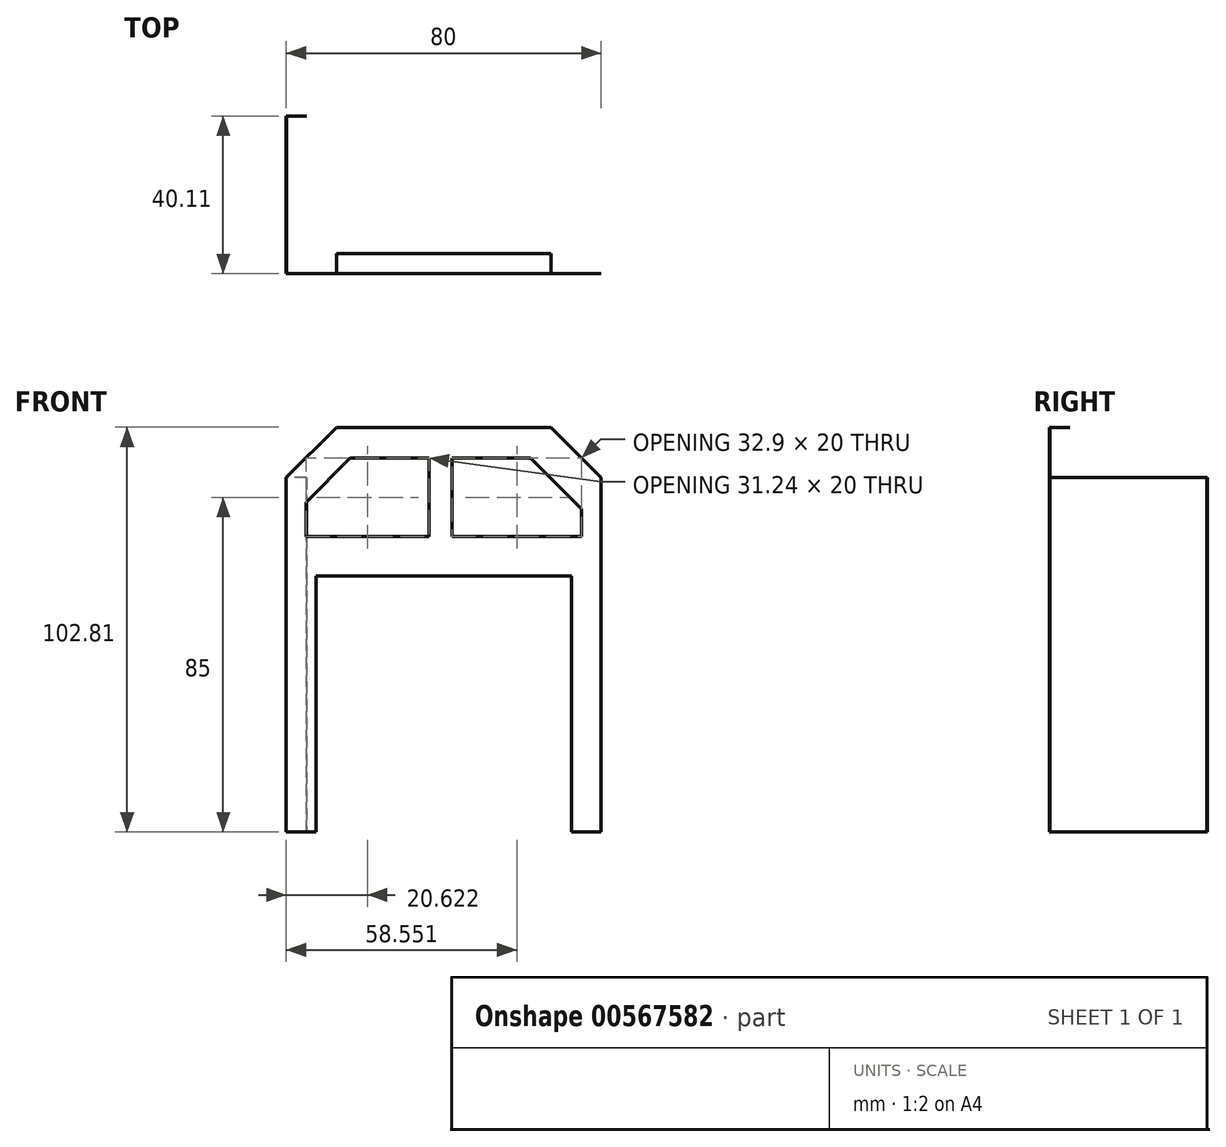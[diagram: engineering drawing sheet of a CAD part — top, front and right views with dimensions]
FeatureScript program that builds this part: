
annotation { "Feature Type Name" : "Feature", "Feature Type Description" : "" }
export const myFeature = defineFeature(function(context is Context, id is Id, definition is map)
    precondition{}
    {
        {
            var Q0;
            Q0=qCreatedBy(makeId("Front.planeOp"),FACE);
            var sketch = newSketch(context, id + "F0", { "sketchPlane" : qUnion([Q0])});
            skLineSegment(sketch, "E0", {"start": v(0, 0) * mm, "end": v(12.8, 12.8) * mm});
            skLineSegment(sketch, "E1", {"start": v(12.8, 12.8) * mm, "end": v(67.2, 12.8) * mm});
            skLineSegment(sketch, "E2", {"start": v(67.2, 12.8) * mm, "end": v(80, 0) * mm});
            skLineSegment(sketch, "E3", {"start": v(80, 0) * mm, "end": v(80, -90) * mm});
            skLineSegment(sketch, "E4", {"start": v(80, -90) * mm, "end": v(72.5, -90) * mm});
            skLineSegment(sketch, "E5", {"start": v(72.5, -90) * mm, "end": v(72.5, -25) * mm});
            skLineSegment(sketch, "E6", {"start": v(72.5, -25) * mm, "end": v(7.5, -25) * mm});
            skLineSegment(sketch, "E7", {"start": v(7.5, -25) * mm, "end": v(7.5, -90) * mm});
            skLineSegment(sketch, "E8", {"start": v(7.5, -90) * mm, "end": v(0, -90) * mm});
            skLineSegment(sketch, "E9", {"start": v(0, -90) * mm, "end": v(0, 0) * mm});
            skLineSegment(sketch, "E10", {"start": v(36.24, 5) * mm, "end": v(36.24, -15) * mm});
            skLineSegment(sketch, "E11", {"start": v(36.24, -15) * mm, "end": v(5, -15) * mm});
            skLineSegment(sketch, "E12", {"start": v(5, -15) * mm, "end": v(5, -6.24) * mm});
            skLineSegment(sketch, "E13", {"start": v(5, -6.24) * mm, "end": v(16.24, 5) * mm});
            skLineSegment(sketch, "E14", {"start": v(16.24, 5) * mm, "end": v(36.24, 5) * mm});
            skLineSegment(sketch, "E15", {"start": v(42.1, 5) * mm, "end": v(42.1, -15) * mm});
            skLineSegment(sketch, "E16", {"start": v(42.1, -15) * mm, "end": v(75, -15) * mm});
            skLineSegment(sketch, "E17", {"start": v(75, -15) * mm, "end": v(75, -7.9) * mm});
            skLineSegment(sketch, "E18", {"start": v(75, -7.9) * mm, "end": v(62.1, 5) * mm});
            skLineSegment(sketch, "E19", {"start": v(62.1, 5) * mm, "end": v(42.1, 5) * mm});
            skSolve(sketch);
        }
        {
            var Q0;
            Q0=makeQuery(id+"F0.imprint","IMPRINT",FACE,{"disambiguationData":[TD([[makeQuery(id+"F0.imprint","IMPRINT",EDGE,{"derivedFrom":sQuery(id+"F0.wireOp",EDGE,"E0")}),-1.0]])]});
            extrude(context, id + "F1", {"entities" : qUnion([Q0]), "depth" : 0.1 * mm, "offsetDistance" : 25 * mm});
        }
        {
            var Q0;
            Q0=makeQuery(id+"F1.opExtrude","CAP_FACE",FACE,{"disambiguationData":[OSD([sQuery(id+"F0.wireOp",EDGE,"E0"),sQuery(id+"F0.wireOp",EDGE,"E1"),sQuery(id+"F0.wireOp",EDGE,"E2"),sQuery(id+"F0.wireOp",EDGE,"E3"),sQuery(id+"F0.wireOp",EDGE,"E4"),sQuery(id+"F0.wireOp",EDGE,"E5"),sQuery(id+"F0.wireOp",EDGE,"E6"),sQuery(id+"F0.wireOp",EDGE,"E7"),sQuery(id+"F0.wireOp",EDGE,"E8"),sQuery(id+"F0.wireOp",EDGE,"E9"),sQuery(id+"F0.wireOp",EDGE,"E10"),sQuery(id+"F0.wireOp",EDGE,"E11"),sQuery(id+"F0.wireOp",EDGE,"E12"),sQuery(id+"F0.wireOp",EDGE,"E13"),sQuery(id+"F0.wireOp",EDGE,"E14"),sQuery(id+"F0.wireOp",EDGE,"E15"),sQuery(id+"F0.wireOp",EDGE,"E16"),sQuery(id+"F0.wireOp",EDGE,"E17"),sQuery(id+"F0.wireOp",EDGE,"E18"),sQuery(id+"F0.wireOp",EDGE,"E19")])],"isStart":true});
            var sketch = newSketch(context, id + "F2", { "sketchPlane" : qUnion([Q0])});
            skLineSegment(sketch, "E20", {"start": v(-79.9, -90) * mm, "end": v(-79.9, 0) * mm});
            skLineSegment(sketch, "E21", {"start": v(-79.89, 0) * mm, "end": v(-80, 0) * mm});
            skLineSegment(sketch, "E22", {"start": v(-80, -90) * mm, "end": v(-79.89, -90) * mm});
            skLineSegment(sketch, "E23", {"start": v(0, -90) * mm, "end": v(-0.1, -90) * mm});
            skLineSegment(sketch, "E24", {"start": v(-0.1, -90) * mm, "end": v(-0.1, 0) * mm});
            skLineSegment(sketch, "E25", {"start": v(-0.1, 0) * mm, "end": v(0, 0) * mm});
            skSolve(sketch);
        }
        {
            var Q0;
            Q0=makeQuery(id+"F2.imprint","IMPRINT",FACE,{"disambiguationData":[TD([[makeQuery(id+"F2.imprint","IMPRINT",EDGE,{"derivedFrom":sQuery(id+"F2.wireOp",EDGE,"E23")}),1.0]])]});
            extrude(context, id + "F3", {"entities" : qUnion([Q0]), "operationType" : NewBodyOperationType.ADD, "depth" : 40 * mm, "offsetDistance" : 25 * mm});
        }
        {
            var Q0;
            Q0=makeQuery(id+"F3.opExtrude","SWEPT_FACE",FACE,{"disambiguationData":[OSD([sQuery(id+"F2.wireOp",EDGE,"E24")])]});
            var sketch = newSketch(context, id + "F4", { "sketchPlane" : qUnion([Q0])});
            skLineSegment(sketch, "E26", {"start": v(40, 0) * mm, "end": v(39.89, 0) * mm});
            skLineSegment(sketch, "E27", {"start": v(39.89, 0) * mm, "end": v(39.9, -90) * mm});
            skSolve(sketch);
        }
        {
            var Q0;
            Q0=makeQuery(id+"F4.imprint","IMPRINT",FACE,{"disambiguationData":[TD([[makeQuery(id+"F4.imprint","IMPRINT",EDGE,{"derivedFrom":sQuery(id+"F4.wireOp",EDGE,"E26")}),1.0]])]});
            extrude(context, id + "F5", {"entities" : qUnion([Q0]), "operationType" : NewBodyOperationType.ADD, "depth" : 5 * mm, "offsetDistance" : 25 * mm});
        }
        {
            var Q0;
            Q0=makeQuery(id+"F1.opExtrude","CAP_FACE",FACE,{"disambiguationData":[OSD([sQuery(id+"F0.wireOp",EDGE,"E0"),sQuery(id+"F0.wireOp",EDGE,"E1"),sQuery(id+"F0.wireOp",EDGE,"E2"),sQuery(id+"F0.wireOp",EDGE,"E3"),sQuery(id+"F0.wireOp",EDGE,"E4"),sQuery(id+"F0.wireOp",EDGE,"E5"),sQuery(id+"F0.wireOp",EDGE,"E6"),sQuery(id+"F0.wireOp",EDGE,"E7"),sQuery(id+"F0.wireOp",EDGE,"E8"),sQuery(id+"F0.wireOp",EDGE,"E9"),sQuery(id+"F0.wireOp",EDGE,"E10"),sQuery(id+"F0.wireOp",EDGE,"E11"),sQuery(id+"F0.wireOp",EDGE,"E12"),sQuery(id+"F0.wireOp",EDGE,"E13"),sQuery(id+"F0.wireOp",EDGE,"E14"),sQuery(id+"F0.wireOp",EDGE,"E15"),sQuery(id+"F0.wireOp",EDGE,"E16"),sQuery(id+"F0.wireOp",EDGE,"E17"),sQuery(id+"F0.wireOp",EDGE,"E18"),sQuery(id+"F0.wireOp",EDGE,"E19")])],"isStart":true});
            var sketch = newSketch(context, id + "F6", { "sketchPlane" : qUnion([Q0])});
            skLineSegment(sketch, "E28.0", {"start": v(-12.8, 12.7) * mm, "end": v(-67.2, 12.7) * mm});
            skLineSegment(sketch, "E29", {"start": v(-67.2, 12.8) * mm, "end": v(-67.2, 12.7) * mm});
            skLineSegment(sketch, "E30", {"start": v(-12.8, 12.8) * mm, "end": v(-12.8, 12.7) * mm});
            skSolve(sketch);
        }
        {
            var Q0;
            Q0=makeQuery(id+"F6.imprint","IMPRINT",FACE,{"disambiguationData":[TD([[makeQuery(id+"F6.imprint","IMPRINT",EDGE,{"derivedFrom":sQuery(id+"F6.wireOp",EDGE,"E28.0")}),-1.0]])]});
            extrude(context, id + "F7", {"entities" : qUnion([Q0]), "operationType" : NewBodyOperationType.ADD, "depth" : 5 * mm, "offsetDistance" : 25 * mm});
        }
    });
